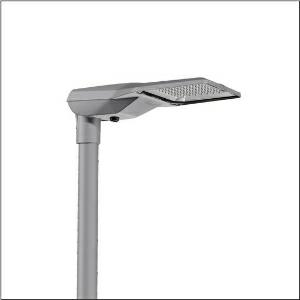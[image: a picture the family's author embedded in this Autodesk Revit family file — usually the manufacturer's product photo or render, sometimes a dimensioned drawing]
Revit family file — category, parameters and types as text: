
# Revit family: streetlight_sl_21_midi___p0_8a_5xe3u33r08nb_1bfe
name_source: partatom
category: Lighting Fixtures
units: mm (PartAtom-declared; Revit-internal decimal feet)

## family parameters
Cut with Voids When Loaded = No
Host = Face
Light Source = No
Part Type = Normal
Room Calculation Point = No
Round Connector Dimension = Use Diameter
Shared = No

## types (1)
- --- (1 x LED, 22900 lm, 151.2 W, 3000K)
    Apparent Load = 151 VA
    CIE Flux Codes = 36 69 97 100 100
    Color Rendering = 70
    Color Temperature = 3000K
    Default Elevation = 1800 mm
    Description = Streetlight SL 21 midi, mast luminaire, primary light control with lens, of PMMA, primary optical cover: cover, of toughened safety glass, transparent, light distribution: P0.8a, light emission: direct distribution, primary light characteristic: asymmetric, installation type: post-top, side-entry, LED, High Power LED, rated luminous flux: 22.900lm, luminous efficacy: 152lm/W, light colour: 730, colour temperature: 3000K, control gear: D4i, control: pre-setting: logarithmic dimming characteristic, flexible luminous flux parameterisation, time-dependent luminous flux control, constant luminous flux control, overheat protection, mains connection: 230..240V, AC, 50/60Hz, start of lifetime: 151W, end of service life: 157W, reduction: 70W, luminaire housing, of diecast aluminium, powder-coated, SITECO metallic grey (DB 702S), corrosivity category C5 high according to DIN EN ISO 12944, multi-level sealing system, sealing non-destructively replaceable, inclination adjustable: 0°, 5°, 10°, 15°, please order mast flange separately, length: 644mm, width: 335mm, height: 110mm, mast flange for spigot size: 42mm (side-entry): 5XC10008XM4, 60/48mm (side-entry/post-top): 5XC10108XM2, 76/60mm (side-entry/post-top): 5XC10108XM1, mounting height: 4..8m, Smart Interface below, protection rating (complete): IP66, insulation class (complete): insulation class II (safety insulation), certification: CE, ENEC, ENEC+, VDE, impact resistance: IK10, permissible operating ambient temperature for outdoor applications: -40..+50°C, standard-compliant lighting for roads and squares, packaging unit: 1 piece

Light Distribution: P0.8a
    Height = 111 mm
    Lamp = 1 x LED
    Lamp Light Flux = 22900 lm
    Lamp Power = 151.2 W
    Lamp count = 1
    Length = 644 mm
    Luminous efficacy = 151 lm/W
    Manufacturer = Siteco
    ModVariant = No
    Model = 5XE3U33R08NB
    Number of Poles = 1
    OnlyDefault = Yes
    Power Factor = 1
    Product Name = Streetlight SL 21 midi | P0.8a
    Product group = mast luminaire | pylon top
    ProductGroupID = 6100
    Protection Class = Protection class II
    Protection Degree = IP 66
    RLX_Detail_Level = 1
    RLX_Emergency_Light_Flux = 0 lm
    RLX_Emergency_Type = 0
    RLX_Emergency_Type_DB = No
    RlxData = <blob elided: 90589 chars, md5=fb1bd027>
    Socket = socket
    Standby Power = 0 W
    System Light Flux = 22901 lm
    System Power = 151 W
    Type Comments = factory setting: luminous flux: 100 % | dim-lin: 254 | 802 mA
    Type Image = l_1004300.jpg
    URL = http://relux.com
    VarID = @adj_079219
    Voltage = 0 V
    Weight = 0.00 kg
    Width = 336 mm

## geometry (parser evidence)
native form markers: Blend x4, Sweep x12
no freeform markers — native parametric forms only
